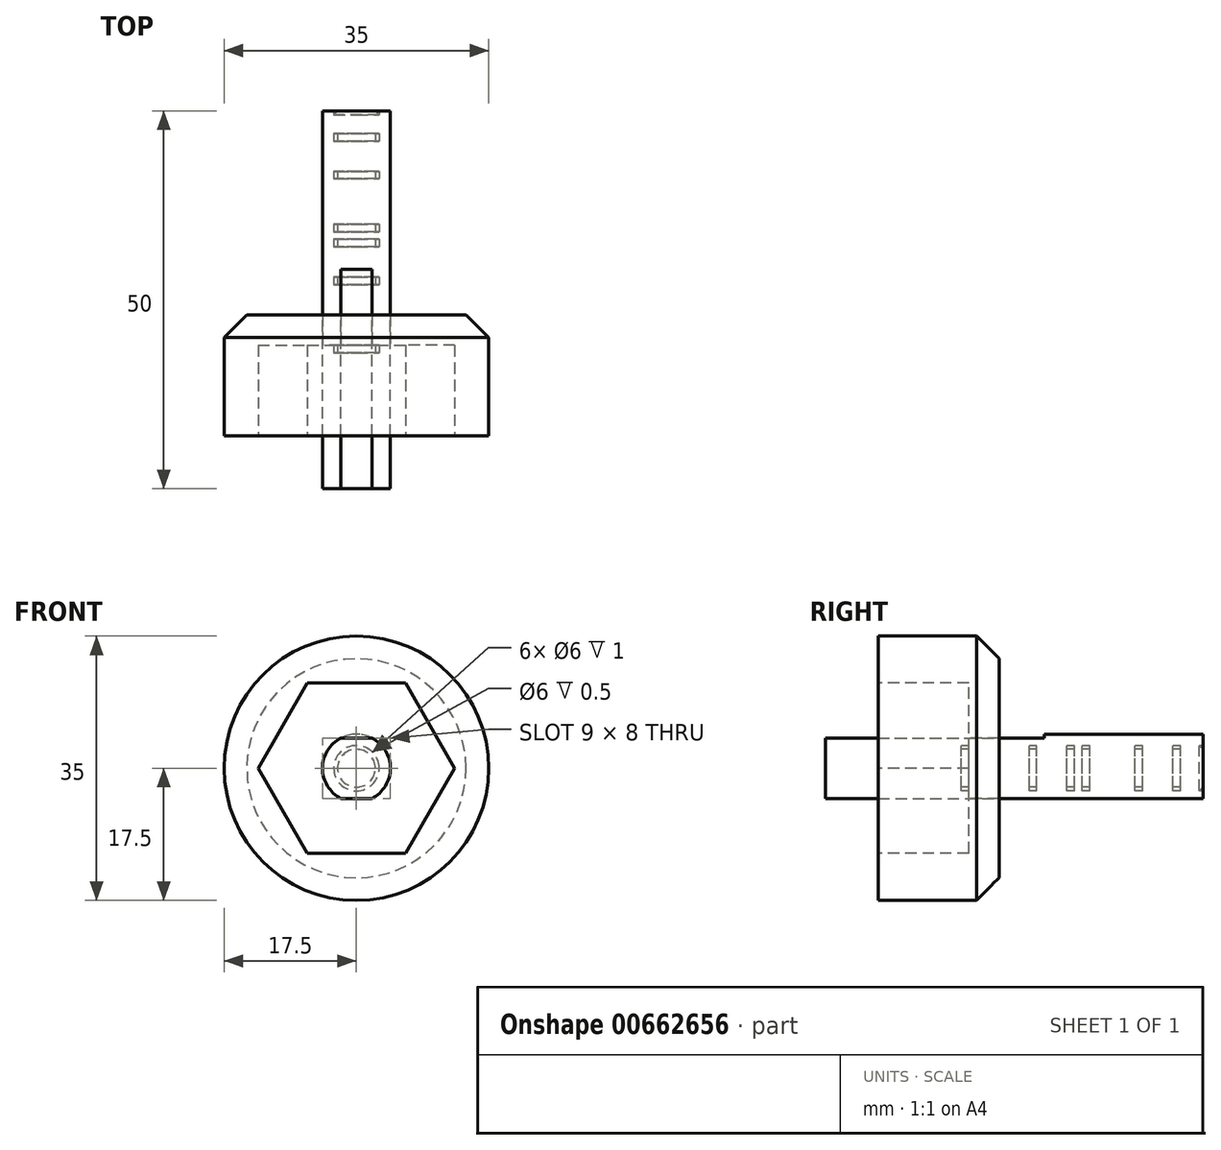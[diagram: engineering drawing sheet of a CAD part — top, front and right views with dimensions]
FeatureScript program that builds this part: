
annotation { "Feature Type Name" : "Feature", "Feature Type Description" : "" }
export const myFeature = defineFeature(function(context is Context, id is Id, definition is map)
    precondition{}
    {
        {
            var Q0;
            Q0=qCreatedBy(makeId("Front.planeOp"),FACE);
            var sketch = newSketch(context, id + "F0", { "sketchPlane" : qUnion([Q0])});
            skArc(sketch, "E0", {"start": v(-15.92, 7.26) * mm, "mid": v(8.75, -15.16) * mm, "end": v(1.67, 17.42) * mm});
            skCircle(sketch, "E1.cCircle", {"center": v(0, 0) * mm, "radius": 11.26 * mm, "construction": true});
            skLineSegment(sketch, "E1.0", {"start": v(-6.5, 11.26) * mm, "end": v(6.5, 11.26) * mm});
            skLineSegment(sketch, "E1.1", {"start": v(6.5, 11.26) * mm, "end": v(13, 0) * mm});
            skLineSegment(sketch, "E1.2", {"start": v(13, 0) * mm, "end": v(6.5, -11.26) * mm});
            skLineSegment(sketch, "E1.3", {"start": v(6.5, -11.26) * mm, "end": v(-6.5, -11.26) * mm});
            skLineSegment(sketch, "E1.4", {"start": v(-6.5, -11.26) * mm, "end": v(-13, 0) * mm});
            skLineSegment(sketch, "E1.5", {"start": v(-13, 0) * mm, "end": v(-6.5, 11.26) * mm});
            skPoint(sketch, "E1.0.midPoint", {"position": v(0, 11.26) * mm});
            skLineSegment(sketch, "E2", {"start": v(-2.06, 4) * mm, "end": v(2.06, 4) * mm});
            skLineSegment(sketch, "E3", {"start": v(-13, -7.5) * mm, "end": v(0, 0) * mm, "construction": true});
            skArc(sketch, "E4.trimOffspring", {"start": v(1.67, 17.42) * mm, "mid": v(-8.75, 15.16) * mm, "end": v(-15.92, 7.26) * mm});
            skCircle(sketch, "E5.converted", {"center": v(0, 0) * mm, "radius": 4.5 * mm});
            skLineSegment(sketch, "E6.MirrorCS", {"start": v(-2.06, -4) * mm, "end": v(2.06, -4) * mm});
            skSolve(sketch);
        }
        {
            var Q0;
            Q0=makeQuery(id+"F0.imprint","IMPRINT",FACE,{"disambiguationData":[TD([[makeQuery(id+"F0.imprint","IMPRINT",EDGE,{"derivedFrom":sQuery(id+"F0.wireOp",EDGE,"E0")}),1.0]])]});
            var Q1;
            Q1=makeQuery(id+"F0.imprint","IMPRINT",FACE,{"disambiguationData":[TD([[makeQuery(id+"F0.imprint","IMPRINT",EDGE,{"derivedFrom":sQuery(id+"F0.wireOp",EDGE,"Cpjcu0II-7CTv-eYmy-ziGy-dCTUWfLcoY72")}),-1.0]])]});
            var Q2;
            Q2=makeQuery(id+"F0.imprint","IMPRINT",FACE,{"disambiguationData":[TD([[makeQuery(id+"F0.imprint","IMPRINT",EDGE,{"derivedFrom":sQuery(id+"F0.wireOp",EDGE,"E1.0")}),-1.0]])]});
            var Q3;
            {var subQ0=sQuery(id+"F0.wireOp",EDGE,"E2");Q3=makeQuery(id+"F0.imprint","IMPRINT",FACE,{"disambiguationData":[TD([[makeQuery(id+"F0.imprint","IMPRINT",EDGE,{"derivedFrom":subQ0}),1.0]])]});}
            var Q4;
            {var subQ0=sQuery(id+"F0.wireOp",EDGE,"E6.MirrorCS");Q4=makeQuery(id+"F0.imprint","IMPRINT",FACE,{"disambiguationData":[TD([[makeQuery(id+"F0.imprint","IMPRINT",EDGE,{"derivedFrom":subQ0}),-1.0]])]});}
            extrude(context, id + "F1", {"entities" : qUnion([Q0, Q1, Q2, Q3, Q4]), "oppositeDirection" : true, "depth" : 16 * mm, "offsetDistance" : 25 * mm});
        }
        {
            var Q0;
            Q0=makeQuery(id+"F0.imprint","IMPRINT",FACE,{"disambiguationData":[TD([[makeQuery(id+"F0.imprint","IMPRINT",EDGE,{"derivedFrom":sQuery(id+"F0.wireOp",EDGE,"E1.0")}),-1.0]])]});
            var Q1;
            {var subQ0=sQuery(id+"F0.wireOp",EDGE,"E2");Q1=makeQuery(id+"F0.imprint","IMPRINT",FACE,{"disambiguationData":[TD([[makeQuery(id+"F0.imprint","IMPRINT",EDGE,{"derivedFrom":subQ0}),1.0]])]});}
            var Q2;
            {var subQ0=sQuery(id+"F0.wireOp",EDGE,"E6.MirrorCS");Q2=makeQuery(id+"F0.imprint","IMPRINT",FACE,{"disambiguationData":[TD([[makeQuery(id+"F0.imprint","IMPRINT",EDGE,{"derivedFrom":subQ0}),-1.0]])]});}
            extrude(context, id + "F2", {"entities" : qUnion([Q0, Q1, Q2]), "operationType" : NewBodyOperationType.REMOVE, "oppositeDirection" : true, "depth" : 12 * mm, "offsetDistance" : 25 * mm});
        }
        {
            var Q0;
            Q0=makeQuery(id+"F1.opExtrude","CAP_EDGE",EDGE,{"disambiguationData":[OSD([sQuery(id+"F0.wireOp",EDGE,"E4.trimOffspring")])],"isStart":false});
            var Q1;
            Q1=makeQuery(id+"F1.opExtrude","CAP_EDGE",EDGE,{"disambiguationData":[OSD([sQuery(id+"F0.wireOp",EDGE,"E0")])],"isStart":false});
            chamfer(context, id + "F3", {"entities" : qUnion([Q0, Q1]), "width" : 3 * mm, "tangentPropagation" : true});
        }
        {
            var Q0;
            {var subQ0=sQuery(id+"F0.wireOp",EDGE,"E2");Q0=makeQuery(id+"F0.imprint","IMPRINT",FACE,{"disambiguationData":[TD([[makeQuery(id+"F0.imprint","IMPRINT",EDGE,{"derivedFrom":subQ0}),-1.0]])]});}
            extrude(context, id + "F4", {"entities" : qUnion([Q0]), "depth" : 7 * mm, "offsetDistance" : 25 * mm, "hasSecondDirection" : true, "secondDirectionOppositeDirection" : true, "secondDirectionDepth" : 22 * mm});
        }
        {
            var Q0;
            {var subQ0=sQuery(id+"F0.wireOp",EDGE,"E2");Q0=makeQuery(id+"F0.imprint","IMPRINT",FACE,{"disambiguationData":[TD([[makeQuery(id+"F0.imprint","IMPRINT",EDGE,{"derivedFrom":subQ0}),-1.0]])]});}
            var Q1;
            {var subQ0=sQuery(id+"F0.wireOp",EDGE,"E2");Q1=makeQuery(id+"F0.imprint","IMPRINT",FACE,{"disambiguationData":[TD([[makeQuery(id+"F0.imprint","IMPRINT",EDGE,{"derivedFrom":subQ0}),1.0]])]});}
            extrude(context, id + "F5", {"entities" : qUnion([Q0, Q1]), "operationType" : NewBodyOperationType.ADD, "oppositeDirection" : true, "depth" : 43 * mm, "offsetDistance" : 25 * mm, "hasSecondDirection" : true, "secondDirectionOppositeDirection" : true, "secondDirectionDepth" : 22 * mm});
        }
        {
            var Q0;
            Q0=qCreatedBy(makeId("Right.planeOp"),FACE);
            var sketch = newSketch(context, id + "F6", { "sketchPlane" : qUnion([Q0])});
            skLineSegment(sketch, "E7.0", {"start": v(-7, 4) * mm, "end": v(-7, -4) * mm});
            skLineSegment(sketch, "E8.bottom", {"start": v(12, -3) * mm, "end": v(11, -3) * mm});
            skLineSegment(sketch, "E8.top", {"start": v(12, -2.5) * mm, "end": v(11, -2.5) * mm});
            skLineSegment(sketch, "E8.left", {"start": v(12, -2.5) * mm, "end": v(12, -3) * mm});
            skLineSegment(sketch, "E8.right", {"start": v(11, -2.5) * mm, "end": v(11, -3) * mm});
            skLineSegment(sketch, "E9.bottom", {"start": v(20, -3) * mm, "end": v(21, -3) * mm});
            skLineSegment(sketch, "E9.top", {"start": v(20, -2.5) * mm, "end": v(21, -2.5) * mm});
            skLineSegment(sketch, "E9.left", {"start": v(20, -3) * mm, "end": v(20, -2.5) * mm});
            skLineSegment(sketch, "E9.right", {"start": v(21, -3) * mm, "end": v(21, -2.5) * mm});
            skLineSegment(sketch, "E10.bottom", {"start": v(25, -3) * mm, "end": v(26, -3) * mm});
            skLineSegment(sketch, "E10.top", {"start": v(25, -2.5) * mm, "end": v(26, -2.5) * mm});
            skLineSegment(sketch, "E10.left", {"start": v(25, -3) * mm, "end": v(25, -2.5) * mm});
            skLineSegment(sketch, "E10.right", {"start": v(26, -3) * mm, "end": v(26, -2.5) * mm});
            skLineSegment(sketch, "E11.bottom", {"start": v(27, -3) * mm, "end": v(28, -3) * mm});
            skLineSegment(sketch, "E11.top", {"start": v(27, -2.5) * mm, "end": v(28, -2.5) * mm});
            skLineSegment(sketch, "E11.left", {"start": v(27, -3) * mm, "end": v(27, -2.5) * mm});
            skLineSegment(sketch, "E11.right", {"start": v(28, -3) * mm, "end": v(28, -2.5) * mm});
            skLineSegment(sketch, "E12.bottom", {"start": v(34, -2.5) * mm, "end": v(35, -2.5) * mm});
            skLineSegment(sketch, "E12.top", {"start": v(34, -3) * mm, "end": v(35, -3) * mm});
            skLineSegment(sketch, "E12.left", {"start": v(34, -2.5) * mm, "end": v(34, -3) * mm});
            skLineSegment(sketch, "E12.right", {"start": v(35, -2.5) * mm, "end": v(35, -3) * mm});
            skLineSegment(sketch, "E13.bottom", {"start": v(39, -3) * mm, "end": v(40, -3) * mm});
            skLineSegment(sketch, "E13.top", {"start": v(39, -2.5) * mm, "end": v(40, -2.5) * mm});
            skLineSegment(sketch, "E13.left", {"start": v(39, -3) * mm, "end": v(39, -2.5) * mm});
            skLineSegment(sketch, "E13.right", {"start": v(40, -3) * mm, "end": v(40, -2.5) * mm});
            skLineSegment(sketch, "E14", {"start": v(43, -2.5) * mm, "end": v(43, -3) * mm});
            skLineSegment(sketch, "E15", {"start": v(43, -3) * mm, "end": v(42.5, -3) * mm});
            skLineSegment(sketch, "E16", {"start": v(42.5, -3) * mm, "end": v(43, -2.5) * mm});
            skSolve(sketch);
        }
        {
            var Q0;
            Q0 = qSketchRegion(id + "F6", true);
            var Q1;
            Q1=makeQuery(id+"F5.opExtrude","CAP_EDGE",EDGE,{"disambiguationData":[OSD([sQuery(id+"F0.wireOp",EDGE,"E5.converted")])],"isStart":false});
            revolve(context, id + "F7", {"operationType" : NewBodyOperationType.REMOVE, "entities" : qUnion([Q0]), "axis" : qUnion([Q1]), "revolveType" : RevolveType.FULL, "oppositeDirection" : true});
        }
    });
